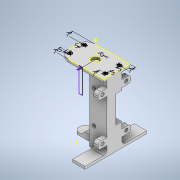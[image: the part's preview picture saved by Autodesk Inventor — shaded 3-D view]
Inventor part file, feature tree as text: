
AUTODESK INVENTOR PART (.ipt)
format: ipt  version: 2020 (Build 240168000, 168)  size: 688,128 bytes
history: native  units: in
note: dims shown in document units (in); Inventor stores cm internally (conversion verified against a paired STEP export)
features: sketch x43, extrude x34, chamfer x8, fillet x7
ambient origin geometry x8: Origin, YZ Plane, XZ Plane, XY Plane, X Axis, Y Axis, Z Axis, Center Point
bodies: Solid1 (feature_tree)
feature tree (92):
  extrude  "Extrusion1"  Depth=1.1811in
  extrude  "Extrusion2"  Depth=0.4724in
  extrude  "Extrusion3"  Depth=0.2362in
  extrude  "Extrusion4"  Depth=0.2756in
  sketch  "Sketch5"  dims[d10=0.2756in d11=0.4724in d12=4.7244in d13=0.0in]
  sketch  "Sketch6"  dims[d14=0.0in]
  extrude  "Extrusion5"  Depth=0.4724in
  fillet  "Fillet7"  Radius=4.7244in
  chamfer  "Chamfer2"  Distance=0.1181in
  chamfer  "Chamfer3"  Distance=0.0787in
  chamfer  "Chamfer4"  Distance=0.1181in Angle=45.0deg
  sketch  "Sketch8"  dims[d15=0.4724in d16=0.1181in d17=0.0in]
  sketch  "Sketch9"  dims[d22=0.7874in]
  extrude  "Extrusion6"  Depth=0.0787in TaperAngle=45.0deg
  sketch  "Sketch11"  dims[d28=0.0197in d32=0.1181in d33=0.0787in d34=45.0deg]
  sketch  "Sketch12"  dims[d35=0.1181in d36=0.0787in d37=45.0deg d38=0.0787in d39=0.0787in d40=45.0deg]
  extrude  "Extrusion7"  TaperAngle=0.0deg  [1 undecoded]
  extrude  "Extrusion8"  Depth=0.5315in
  sketch  "Sketch14"  dims[d41=0.0in d42=0.0in]
  extrude  "Extrusion9"  Depth=0.2165in
  sketch  "Sketch15"  dims[d43=3.937in d44=0.0in d45=0.5315in]
  extrude  "Extrusion10"  Depth=1.4567in
  extrude  "Extrusion11"  Depth=0.5512in
  extrude  "Extrusion12"  Depth=0.1614in
  extrude  "Extrusion13"  Depth=3.937in TaperAngle=0.0deg
  chamfer  "Chamfer5"  Distance=0.4724in
  extrude  "Extrusion14"  Depth=0.126in
  sketch  "Sketch20"  dims[d54=0.1614in d55=3.937in d56=0.0in]
  extrude  "Extrusion15"  TaperAngle=0.0deg  [1 undecoded]
  extrude  "Extrusion16"  TaperAngle=0.0deg  [1 undecoded]
  extrude  "Extrusion17"  Depth=0.1575in
  extrude  "Extrusion18"  TaperAngle=0.0deg  [1 undecoded]
  extrude  "Extrusion19"  Depth=1.4567in
  chamfer  "Chamfer6"  Distance=0.1969in
  fillet  "Fillet8"  Radius=1.378in
  chamfer  "Chamfer7"  Distance=0.1181in
  extrude  "Extrusion20"  TaperAngle=0.0deg  [1 undecoded]
  fillet  "Fillet9"  Radius=0.1181in
  sketch  "Sketch29"  dims[d70=0.1575in d71=0.0in d72=0.0in]
  extrude  "Extrusion21"  Depth=0.0787in TaperAngle=0.0deg
  sketch  "Sketch31"  dims[d75=0.2087in]
  extrude  "Extrusion22"  Depth=0.1969in TaperAngle=0.0deg
  extrude  "Extrusion23"  TaperAngle=0.0deg  [1 undecoded]
  sketch  "Sketch32"  dims[d76=0.9055in d77=0.1969in d78=0.0in d79=1.378in]
  extrude  "Extrusion24"  Depth=0.0787in
  sketch  "Sketch34"  dims[d83=0.7874in d84=0.0in d85=0.1181in d86=0.0in]
  fillet  "Fillet10"  Radius=0.0787in
  extrude  "Extrusion26"  Depth=0.0394in
  extrude  "Extrusion27"  Depth=0.3071in
  fillet  "Fillet12"  Radius=1.378in
  extrude  "Extrusion28"  Depth=0.2362in TaperAngle=0.0deg
  extrude  "Extrusion29"  Depth=0.1575in
  extrude  "Extrusion30"  Depth=0.1181in
  fillet  "Fillet13"  Radius=0.1969in
  extrude  "Extrusion31"  Depth=0.0787in
  extrude  "Extrusion32"  Depth=1.1811in
  chamfer  "Chamfer8"  Distance=1.1811in
  fillet  "Fillet14"  Radius=0.3071in
  chamfer  "Chamfer9"  Distance=0.0787in
  extrude  "Extrusion33"  TaperAngle=0.0deg  [1 undecoded]
  extrude  "Extrusion34"  Depth=0.1181in TaperAngle=0.0deg
  extrude  "Extrusion35"  Depth=0.0197in
  sketch  "Sketch45"  dims[d133=0.2756in d134=1.1811in d135=1.1811in d136=0.0in d137=0.3071in d138=0.0787in d139=0.0in]
  sketch  "Sketch46"  dims[d140=0.0394in d141=0.0in d142=0.0in]
  sketch  "Sketch47"  dims[d143=0.0in d144=0.1181in d145=0.0in d146=0.0197in d147=0.0197in d148=0.0591in d149=0.0591in d152=0.0197in d153=0.3937in d154=0.3937in d155=0.315in d156=0.315in d157=0.315in d158=0.315in d159=0.1969in d160=0.0in d161=0.1969in d162=0.1969in d163=0.1969in d164=0.1969in d165=0.1575in d166=0.1575in d167=0.1575in d168=0.1575in d169=0.126in d170=0.126in d171=0.126in d172=0.126in d173=0.2362in d174=0.0in d176=0.1181in d177=0.0in d178=0.1181in d179=0.5118in d180=0.0in d181=0.1181in d182=0.0787in d183=0.0787in d184=0.1575in d185=0.0in d186=0.7874in d187=0.1575in d188=0.5906in d189=0.0in d190=0.1181in d191=0.0in d192=0.3937in d193=0.3937in d194=0.3937in d195=0.5512in d196=0.1181in d197=0.0in d198=0.315in d199=0.4724in d200=0.1181in d201=0.0in d202=0.1181in d203=0.0787in d204=45.0deg d205=0.0157in d206=0.0787in d207=0.0787in d208=45.0deg d209=0.1732in d210=0.7087in d211=0.2362in d212=0.0787in d213=0.0in d214=0.1969in d215=0.2756in d216=0.1969in d217=0.2756in d218=0.1969in d219=0.2756in d220=0.2756in d221=0.1969in d222=0.1575in d223=0.1575in d224=0.1575in d225=0.1575in d226=0.1181in d227=0.0in d228=0.1339in d229=0.1181in d230=0.0in d231=0.0in]
  sketch  "Sketch1"  dims[d0=3.5433in d1=1.1811in]
  sketch  "Sketch2"  dims[d2=0.4724in d3=0.0in d4=0.3071in]
  sketch  "Sketch3"  dims[d5=0.2362in d6=0.2362in]
  sketch  "Sketch4"  dims[d7=4.7244in d8=0.0in d9=0.2756in]
  sketch  "Sketch10"  dims[d23=0.2953in d24=0.0787in d25=0.0in]
  sketch  "Sketch16"  dims[d46=2.5984in d47=0.2165in]
  sketch  "Sketch17"  dims[d48=0.3543in d49=1.4567in]
  sketch  "Sketch18"  dims[d50=0.5512in d51=0.1457in]
  sketch  "Sketch19"  dims[d52=0.1457in d53=0.1614in]
  sketch  "Sketch21"  dims[d57=0.0787in]
  sketch  "Sketch22"  dims[d58=0.0in d59=0.4724in d60=0.0in]
  sketch  "Sketch25"  dims[d61=0.126in d62=0.126in]
  sketch  "Sketch26"  dims[d63=0.0in d64=0.0in]
  sketch  "Sketch27"  dims[d65=0.2756in d66=0.0in d67=0.0in]
  sketch  "Sketch28"  dims[d68=0.1575in d69=0.1575in]
  sketch  "Sketch30"  dims[d73=0.1614in d74=1.4567in]
  sketch  "Sketch33"  dims[d80=0.5512in d81=0.1181in d82=0.0in]
  sketch  "Sketch35"  dims[d87=0.0787in d88=0.0787in d89=45.0deg d90=0.0787in d91=0.0in]
  sketch  "Sketch36"  dims[d92=0.1575in d93=0.1969in d94=0.0in]
  sketch  "Sketch37"  dims[d95=0.1575in d96=0.0in d107=0.0in]
  sketch  "Sketch38"  dims[d108=0.0787in d109=0.0787in d110=0.0787in]
  sketch  "Sketch39"  dims[d111=0.0394in d112=0.0394in]
  sketch  "Sketch40"  dims[d113=1.378in d114=0.0in d115=0.3071in d116=1.378in d117=0.0in]
  sketch  "Sketch41"  dims[d118=0.1181in d119=0.2362in d120=0.0in]
  sketch  "Sketch42"  dims[d121=0.0787in d122=0.0787in d123=45.0deg d124=0.1575in]
  sketch  "Sketch43"  dims[d125=0.1575in d126=0.0787in d127=45.0deg d128=0.1181in d129=0.1969in]
  sketch  "Sketch44"  dims[d130=1.1811in d131=0.0in d132=0.0787in]
note: 7 required parameter values undecoded (feature->parameter linkage not recoverable at this tier; creation-order binding heuristic only, values carry confidence <= 0.55)
